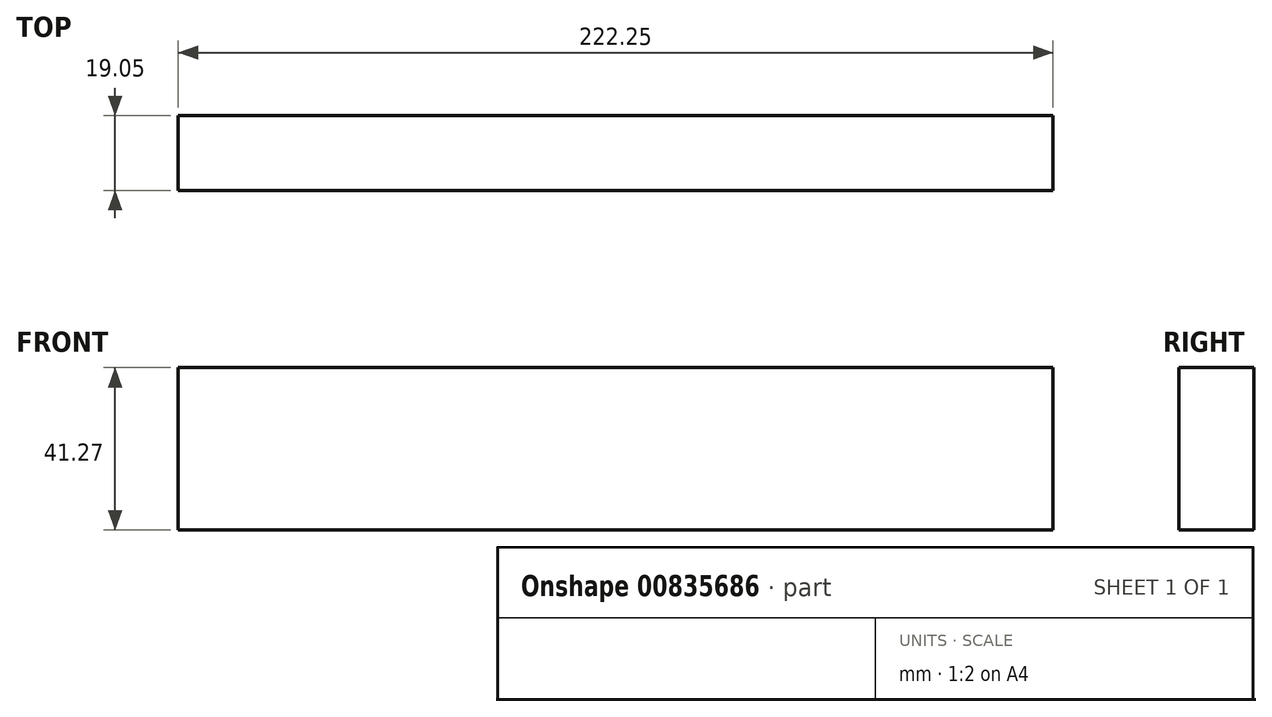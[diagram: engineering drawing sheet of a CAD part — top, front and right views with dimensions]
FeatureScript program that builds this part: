
annotation { "Feature Type Name" : "Feature", "Feature Type Description" : "" }
export const myFeature = defineFeature(function(context is Context, id is Id, definition is map)
    precondition{}
    {
        {
            var Q0;
            Q0=qCreatedBy(makeId("Front.planeOp"),FACE);
            var sketch = newSketch(context, id + "F0", { "sketchPlane" : qUnion([Q0])});
            skLineSegment(sketch, "E0.bottom", {"start": v(0, 0) * mm, "end": v(222.25, 0) * mm});
            skLineSegment(sketch, "E0.top", {"start": v(0, 41.28) * mm, "end": v(222.25, 41.28) * mm});
            skLineSegment(sketch, "E0.left", {"start": v(0, 0) * mm, "end": v(0, 41.28) * mm});
            skLineSegment(sketch, "E0.right", {"start": v(222.25, 0) * mm, "end": v(222.25, 41.28) * mm});
            skSolve(sketch);
        }
        {
            var Q0;
            Q0=qSketchRegion(id+"F0",true);
            extrude(context, id + "F1", {"entities" : qUnion([Q0]), "depth" : 19.05 * mm, "offsetDistance" : 25.4 * mm});
        }
    });
